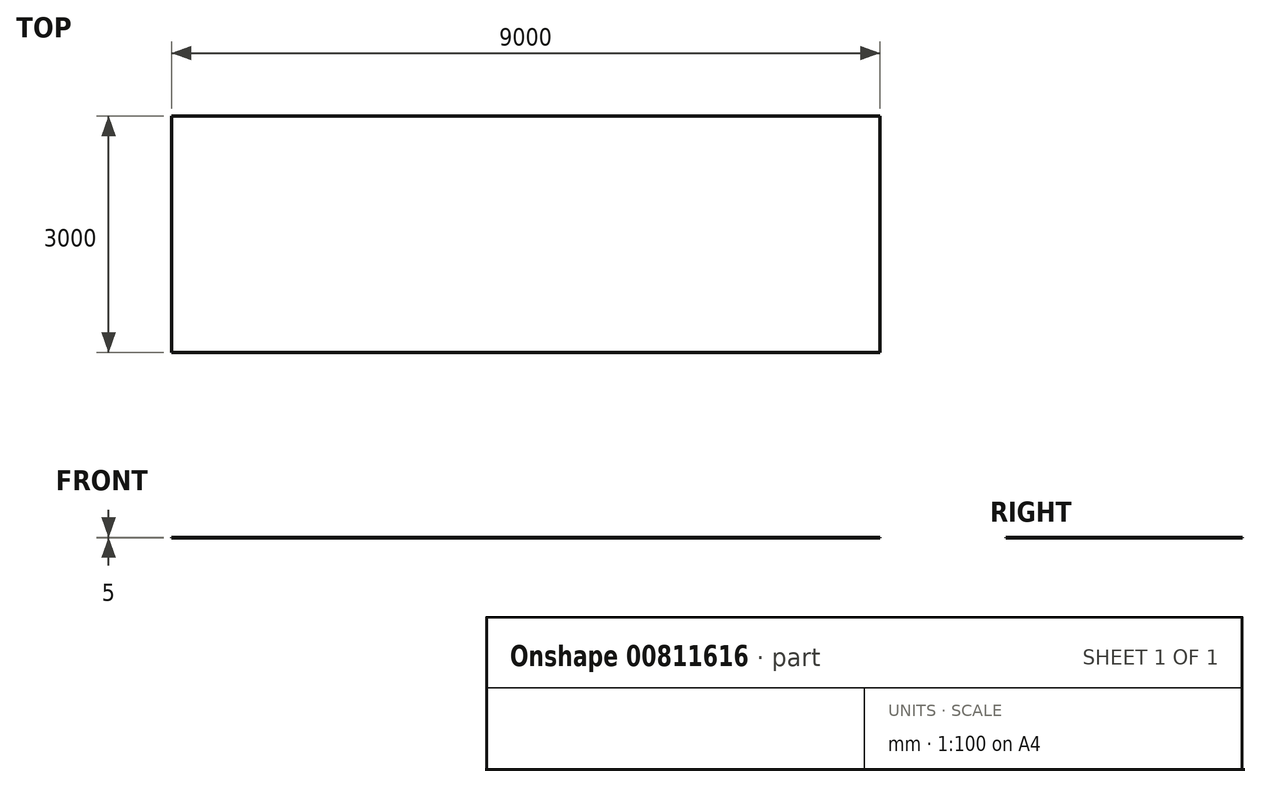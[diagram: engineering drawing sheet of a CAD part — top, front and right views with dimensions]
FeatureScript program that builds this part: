
annotation { "Feature Type Name" : "Feature", "Feature Type Description" : "" }
export const myFeature = defineFeature(function(context is Context, id is Id, definition is map)
    precondition{}
    {
        {
            var Q0;
            Q0=qCreatedBy(makeId("Top.planeOp"),FACE);
            var sketch = newSketch(context, id + "F0", { "sketchPlane" : qUnion([Q0])});
            skLineSegment(sketch, "E0.bottom", {"start": v(-4339.31, 1800.43) * mm, "end": v(4660.69, 1800.43) * mm});
            skLineSegment(sketch, "E0.top", {"start": v(-4339.31, -1199.57) * mm, "end": v(4660.69, -1199.57) * mm});
            skLineSegment(sketch, "E0.left", {"start": v(-4339.31, 1800.43) * mm, "end": v(-4339.31, -1199.57) * mm});
            skLineSegment(sketch, "E0.right", {"start": v(4660.69, 1800.43) * mm, "end": v(4660.69, -1199.57) * mm});
            skSolve(sketch);
        }
        {
            var Q0;
            Q0 = qSketchRegion(id + "F0", true);
            extrude(context, id + "F1", {"entities" : qUnion([Q0]), "depth" : 5 * mm, "offsetDistance" : 25 * mm});
        }
    });
